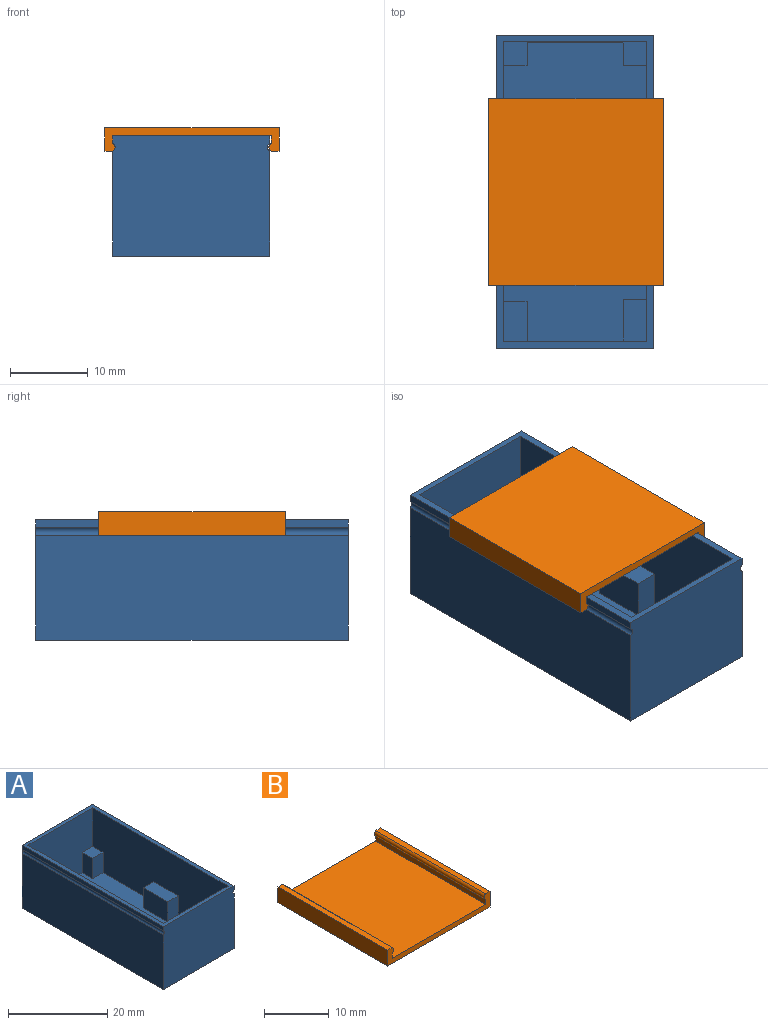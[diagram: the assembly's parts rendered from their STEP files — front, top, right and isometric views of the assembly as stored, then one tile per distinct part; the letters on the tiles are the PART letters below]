
ASSEMBLY  parts=2 mates=1
PART A: 35 faces, bbox 20.2x40.2x15.5 mm
  f0: plane 40.2x1mm, normal (-1,0,0), area 40.2mm2, adj f2,f5,f11,f34
  f1: plane 40.2x1mm, normal (1,0,0), area 40.2mm2, adj f2,f5,f11,f33
  f2: plane 20.2x15.5mm, normal (0,-1,0), area 312.7mm2, adj f0,f1,f3,f4,f6,f11,f33,f34
  f3: plane 40.2x13.5mm, normal (-1,0,0), area 542.7mm2, adj f2,f5,f6,f34
  f4: plane 40.2x13.5mm, normal (1,0,0), area 542.7mm2, adj f2,f5,f6,f33
  f5: plane 20.2x15.5mm, normal (0,1,0), area 312.7mm2, adj f0,f1,f3,f4,f6,f11,f33,f34
  f6: plane 40.2x20.2mm, normal (0,0,-1), area 812mm2, adj f2,f3,f4,f5
  f7: plane 18.4x14.5mm, normal (0,1,0), area 236.8mm2, adj f9,f10,f11,f26,f28,f29,f30,f32
  f8: plane 18.4x14.5mm, normal (0,-1,0), area 236.8mm2, adj f9,f10,f11,f17,f18,f20,f21,f32
  f9: plane 38.6x14.5mm, normal (1,0,0), area 483.5mm2, adj f7,f8,f11,f14,f15,f16,f18,f19
  f10: plane 38.6x14.5mm, normal (-1,0,0), area 482.3mm2, adj f7,f8,f11,f20,f22,f23,f24,f25
  f11: plane 40.2x20.2mm, normal (0,0,1), area 101.8mm2, adj f0,f1,f2,f5,f7,f8,f9,f10
  f12: plane 7x5mm, normal (1,0,0), area 35mm2, adj f14,f15,f16,f32
  f13: plane 7x5mm, normal (-1,0,0), area 35mm2, adj f23,f24,f25,f32
  f14: plane 7x3mm, normal (0,0,1), area 21mm2, adj f9,f12,f15,f16
  f15: plane 5x3mm, normal (0,1,0), area 15mm2, adj f9,f12,f14,f32
  f16: plane 5x3mm, normal (0,-1,0), area 15mm2, adj f9,f12,f14,f32
  f17: plane 5x3mm, normal (1,0,0), area 15mm2, adj f8,f18,f19,f32
  f18: plane 3x3mm, normal (0,0,1), area 9mm2, adj f8,f9,f17,f19
  f19: plane 5x3mm, normal (0,-1,0), area 15mm2, adj f9,f17,f18,f32
  f20: plane 3x3mm, normal (0,0,1), area 9mm2, adj f8,f10,f21,f22
  f21: plane 5x3mm, normal (-1,0,0), area 15mm2, adj f8,f20,f22,f32
  f22: plane 5x3mm, normal (0,-1,0), area 15mm2, adj f10,f20,f21,f32
  f23: plane 7x3mm, normal (0,0,1), area 21mm2, adj f10,f13,f24,f25
  f24: plane 5x3mm, normal (0,-1,0), area 15mm2, adj f10,f13,f23,f32
  f25: plane 5x3mm, normal (0,1,0), area 15mm2, adj f10,f13,f23,f32
  f26: plane 5.49x3mm, normal (0,0,1), area 16.5mm2, adj f7,f10,f27,f28
  f27: plane 5x3mm, normal (0,1,0), area 15mm2, adj f10,f26,f28,f32
  f28: plane 5.49x5mm, normal (-1,0,0), area 27.4mm2, adj f7,f26,f27,f32
  f29: plane 5.23x3mm, normal (0,0,1), area 15.7mm2, adj f7,f9,f30,f31
  f30: plane 5.23x5mm, normal (1,0,0), area 26.2mm2, adj f7,f29,f31,f32
  f31: plane 5x3mm, normal (0,1,0), area 15mm2, adj f9,f29,f30,f32
  f32: plane 38.6x18.4mm, normal (0,0,1), area 618.1mm2, adj f7,f8,f9,f10,f12,f13,f15,f16
  f33: cylinder r=0.57mm len=40.2mm, axis (0,-1,0), area 49.2mm2, adj f1,f2,f4,f5
  f34: cylinder r=0.57mm len=40.2mm, axis (0,-1,0), area 49.2mm2, adj f0,f2,f3,f5
PART B: 12 faces, bbox 22.4x24x3 mm
  f0: plane 24x1mm, normal (-1,0,0), area 24mm2, adj f2,f3,f5,f11
  f1: plane 24x1mm, normal (1,0,0), area 24mm2, adj f2,f3,f5,f10
  f2: plane 24x20.4mm, normal (0,0,1), area 489.6mm2, adj f0,f1,f3,f5
  f3: plane 22.4x3mm, normal (0,1,0), area 26.8mm2, adj f0,f1,f2,f4,f6,f7,f8,f9
  f4: plane 24x3mm, normal (-1,0,0), area 72mm2, adj f3,f5,f7,f8
  f5: plane 22.4x3mm, normal (0,-1,0), area 26.8mm2, adj f0,f1,f2,f4,f6,f7,f8,f9
  f6: plane 24x3mm, normal (1,0,0), area 72mm2, adj f3,f5,f7,f9
  f7: plane 24x22.4mm, normal (0,0,-1), area 537.6mm2, adj f3,f4,f5,f6
  f8: plane 24x1mm, normal (0,0,1), area 24mm2, adj f3,f4,f5,f10
  f9: plane 24x1mm, normal (0,0,1), area 24mm2, adj f3,f5,f6,f11
  f10: cylinder r=0.57mm len=24mm, axis (0,-1,0), area 29.4mm2, adj f1,f3,f5,f8
  f11: cylinder r=0.57mm len=24mm, axis (0,-1,0), area 29.4mm2, adj f0,f3,f5,f9
PLACE A t=(-0.4,-0.1,-4)mm
PLACE B rot(axis=(1,0,0),180deg) t=(31,-2,12.5)mm
MATE fastened B.f2 <-> A.f11  axis (0,0,-1) through (-0.4,20,11.5)mm
